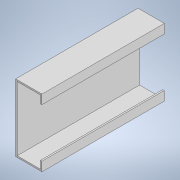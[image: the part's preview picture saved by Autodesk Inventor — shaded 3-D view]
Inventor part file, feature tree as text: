
AUTODESK INVENTOR PART (.ipt)
format: ipt  version: 2020 (Build 240168000, 168)  size: 110,080 bytes
history: native  units: mm
features: extrude x1, sketch x1
ambient origin geometry x8: Origin, YZ Plane, XZ Plane, XY Plane, X Axis, Y Axis, Z Axis, Center Point
bodies: Solid1 (feature_tree)
feature tree (2):
  extrude  "Extrusion1"  Depth=110.0mm
  sketch  "Sketch1"  dims[d0=43.0mm d1=110.0mm d2=15.0mm d3=15.0mm d4=2.5mm d5=200.0mm d6=0.0mm]
